# Revit family: PM4055551-784725551-PM4065551-ducha-greta-mateblack-monocontrol
name_source: partatom
category: Plumbing Fixtures
units: mm (PartAtom-declared; Revit-internal decimal feet)

## family parameters
Always vertical = Yes
Cut with Voids When Loaded = No
Host = Wall
OmniClass Number = 23.31.17.00
Part Type = Normal
Room Calculation Point = No
Round Connector Dimension = Use Diameter
Shared = No

## types (1)
- Ducha monocontrol Palma Pro
    Alto = 108 mm
    Altura ducha = 1850 mm
    Altura mezclador = 1500 mm  [stored 4.92126 ft]
    Ancho = 250 mm  [stored 0.82021 ft]
    Capacidad de flujo = A 60 psi: 6.60 L/min.
    Ciclo de vida de la unidad de cierre = 500000 ciclos.
    Default Elevation = 0 mm  [stored 0 ft]
    Description = La ducha Palma con tecnología de ahorro de agua minimiza el derroche ofreciendo un mayor rendimiento sin sacrificar el confort en la ducha, ofrece mayor cobertura para una mayor relajación, ideal para espacios medianos y consumidores que buscan una cobertura intermedia.
    Dimensiones generales del producto = 250 x 200 x 62.7 mm.
    Diámetro abasto = 13 mm
    Garantía = 30 años Grival - 3 años Cromado.
    Manufacturer = Corona.
    Material = Corona_mate_black
    Material 2 = Corona_Plastico_Gris
    Material 3 = Corona_Acero inoxidable
    Material 4 = Corona_mate_black
    Model = PM4045551_Ducha monocontrol Palma Pro.
    Normatividad = NTC 1644.
    Peso  Bruto = 1437 gr. / 3.16 lb.
    Peso neto = 1227 gr. / 2.27 lb.
    Presión máxima recomendada = 120 psi.
    Presión mínima recomendada = 20 psi.
    Profundidad = 268 mm
    Recubrimientos = Resistente a la corrosión, pelado y decoloración por agua. Producto no tóxico. Producto para uso doméstico.
    Temperaturas máxima de trabajo = 71° C / 159.8° F.
    Temperaturas mínima de trabajo = 5° C / 41° F.

note: [stored X ft] marks values corroborated as IEEE doubles in the binary element streams (Revit-internal decimal feet)

## geometry (parser evidence)
native form markers: Sweep x6
no freeform markers — native parametric forms only
